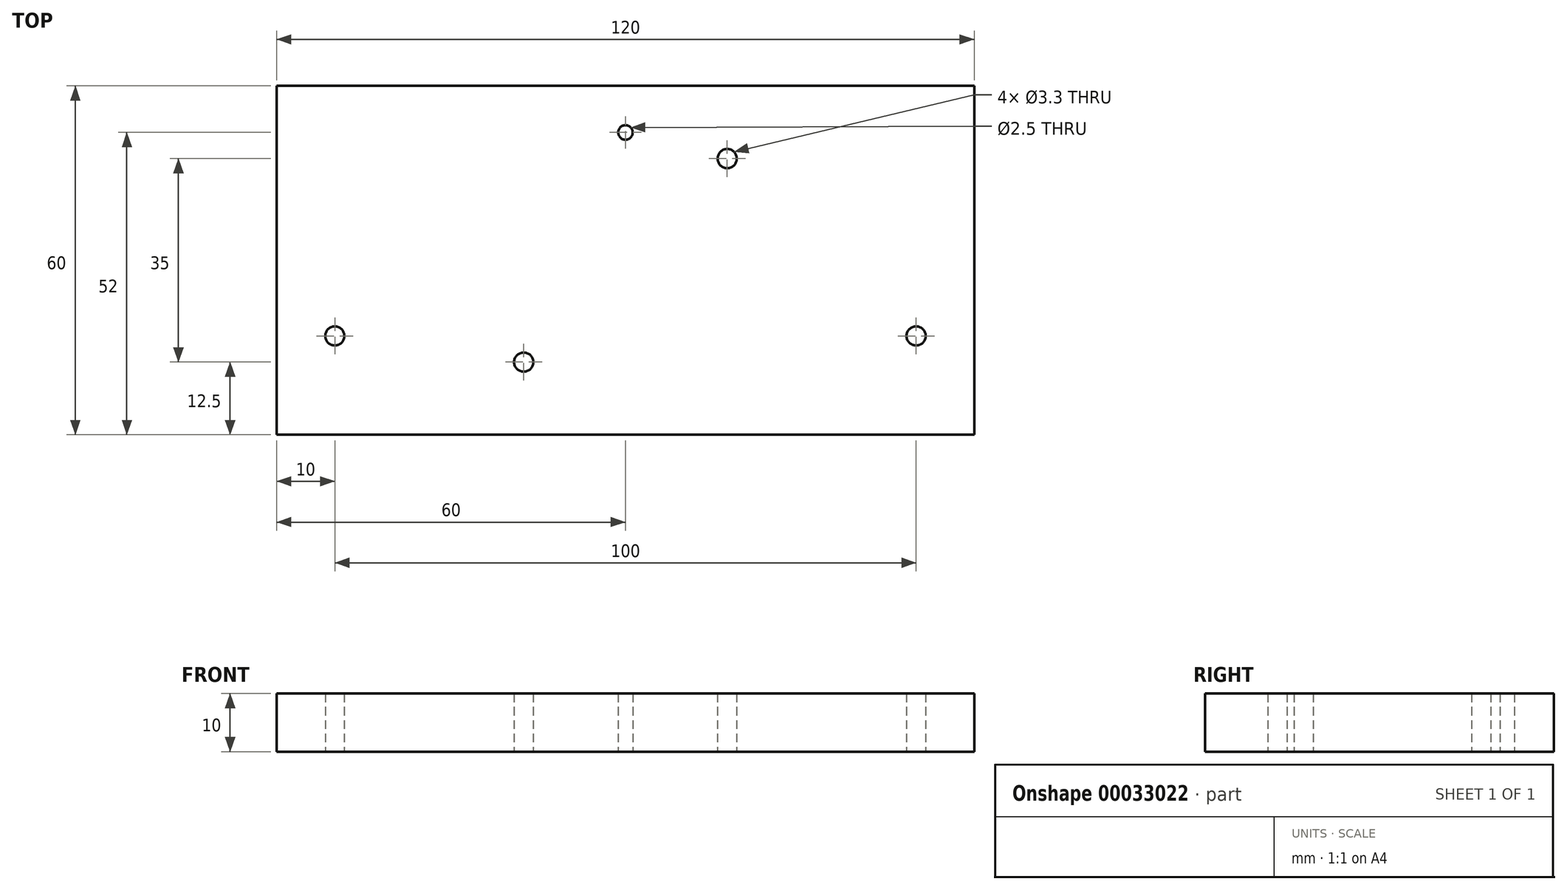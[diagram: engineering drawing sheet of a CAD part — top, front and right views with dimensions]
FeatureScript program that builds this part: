
annotation { "Feature Type Name" : "Feature", "Feature Type Description" : "" }
export const myFeature = defineFeature(function(context is Context, id is Id, definition is map)
    precondition{}
    {
        {
            var Q0;
            Q0=qCreatedBy(makeId("Top.planeOp"),FACE);
            var sketch = newSketch(context, id + "F0", { "sketchPlane" : qUnion([Q0])});
            skLineSegment(sketch, "E0.bottom", {"start": v(-60, 30) * mm, "end": v(60, 30) * mm});
            skLineSegment(sketch, "E0.top", {"start": v(-60, -30) * mm, "end": v(60, -30) * mm});
            skLineSegment(sketch, "E0.left", {"start": v(-60, 30) * mm, "end": v(-60, -30) * mm});
            skLineSegment(sketch, "E0.right", {"start": v(60, 30) * mm, "end": v(60, -30) * mm});
            skCircle(sketch, "E1", {"center": v(0, 22) * mm, "radius": 1.25 * mm});
            skCircle(sketch, "E2", {"center": v(17.5, 17.5) * mm, "radius": 1.65 * mm});
            skCircle(sketch, "E3", {"center": v(-17.5, -17.5) * mm, "radius": 1.65 * mm});
            skCircle(sketch, "E4", {"center": v(-50, -13) * mm, "radius": 1.65 * mm});
            skCircle(sketch, "E5", {"center": v(50, -13) * mm, "radius": 1.65 * mm});
            skLineSegment(sketch, "E6", {"start": v(-79, -13) * mm, "end": v(71.96, -13) * mm, "construction": true});
            skLineSegment(sketch, "E7", {"start": v(-17.5, 39.1) * mm, "end": v(-17.5, -44.92) * mm, "construction": true});
            skLineSegment(sketch, "E8", {"start": v(17.5, 39.61) * mm, "end": v(17.5, -45.93) * mm, "construction": true});
            skLineSegment(sketch, "E9", {"start": v(-78.75, 17.5) * mm, "end": v(73.21, 17.5) * mm, "construction": true});
            skLineSegment(sketch, "E10", {"start": v(-79, -17.5) * mm, "end": v(73.21, -17.5) * mm, "construction": true});
            skSolve(sketch);
        }
        {
            var Q0;
            Q0 = qSketchRegion(id + "F0", true);
            var Q1;
            Q1=makeQuery(id+"F0.imprint","IMPRINT",FACE,{"disambiguationData":[TD([[makeQuery(id+"F0.imprint","IMPRINT",EDGE,{"derivedFrom":sQuery(id+"F0.wireOp",EDGE,"E0.bottom")}),-1.0]])]});
            extrude(context, id + "F1", {"entities" : qUnion([Q0, Q1]), "depth" : 10 * mm});
        }
    });
